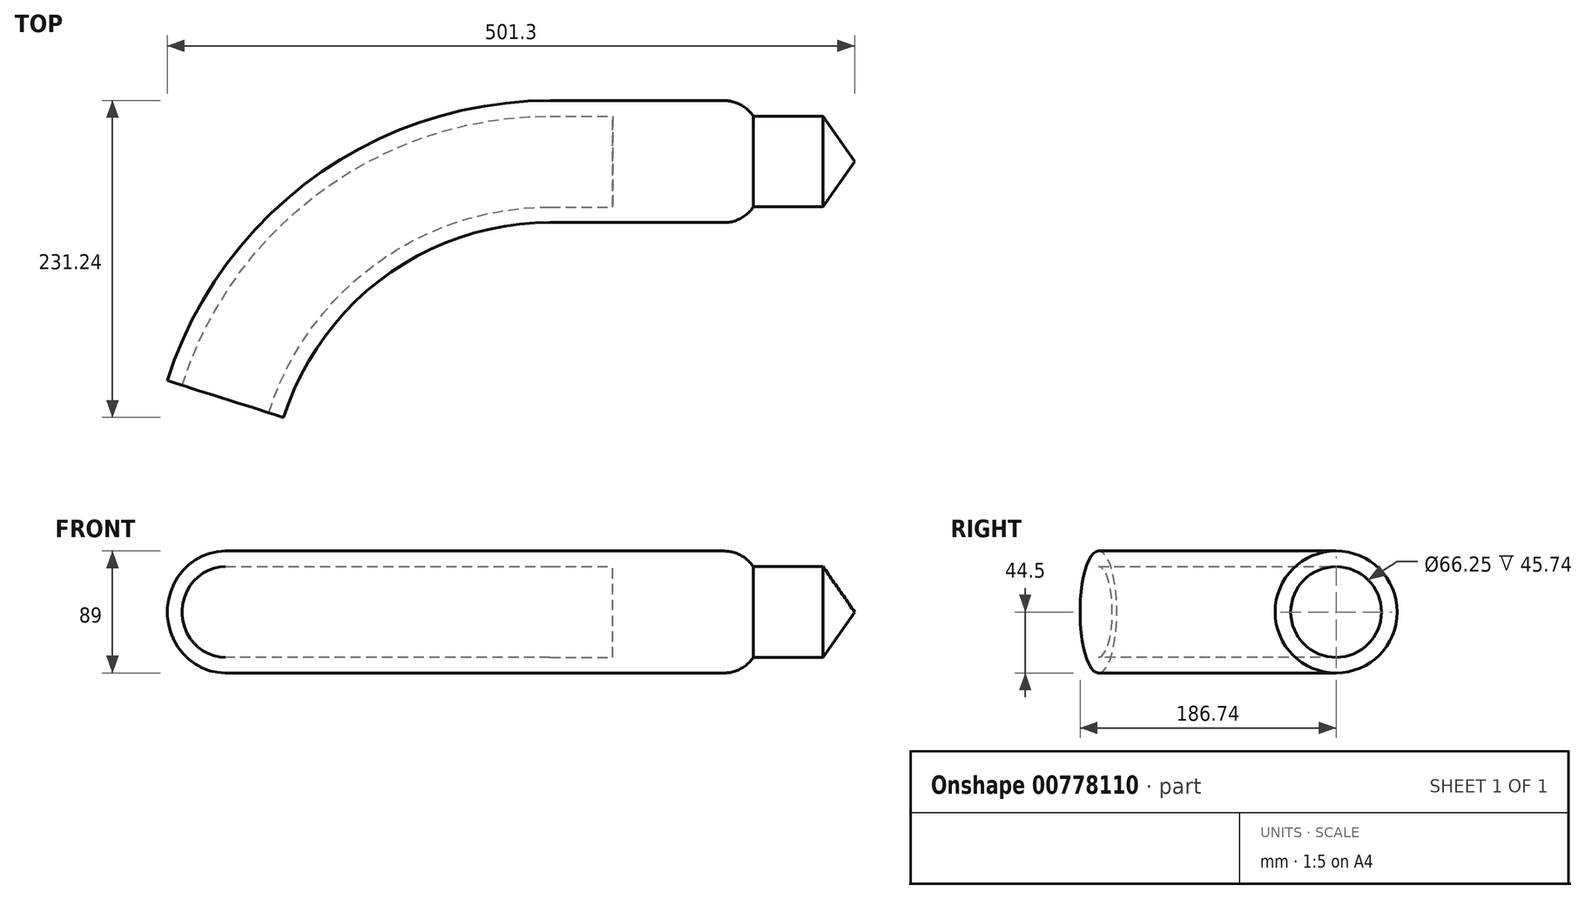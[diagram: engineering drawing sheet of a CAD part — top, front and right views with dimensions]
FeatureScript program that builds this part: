
annotation { "Feature Type Name" : "Feature", "Feature Type Description" : "" }
export const myFeature = defineFeature(function(context is Context, id is Id, definition is map)
    precondition{}
    {
        {
            var Q0;
            Q0=qCreatedBy(makeId("Front.planeOp"),FACE);
            var sketch = newSketch(context, id + "F0", { "sketchPlane" : qUnion([Q0])});
            skLineSegment(sketch, "E0", {"start": v(0, 0) * mm, "end": v(174.67, 0) * mm, "construction": true});
            skLineSegment(sketch, "E1", {"start": v(0, 33.12) * mm, "end": v(0, 44.5) * mm});
            skLineSegment(sketch, "E2", {"start": v(0, 44.5) * mm, "end": v(127.05, 44.5) * mm});
            skArc(sketch, "E3", {"start": v(127.05, 44.5) * mm, "mid": v(139.07, 41.47) * mm, "end": v(148.2, 33.1) * mm});
            skLineSegment(sketch, "E4", {"start": v(148.2, 33.1) * mm, "end": v(199.15, 33.1) * mm});
            skLineSegment(sketch, "E5", {"start": v(199.15, 33.1) * mm, "end": v(222.2, 0) * mm});
            skLineSegment(sketch, "E6", {"start": v(222.2, 0) * mm, "end": v(45.74, 0) * mm});
            skLineSegment(sketch, "E7", {"start": v(0, 33.12) * mm, "end": v(45.74, 33.12) * mm});
            skLineSegment(sketch, "E8", {"start": v(45.74, 33.12) * mm, "end": v(45.74, 0) * mm});
            skSolve(sketch);
        }
        {
            var Q0;
            Q0=makeQuery(id+"F0.imprint","IMPRINT",FACE,{"disambiguationData":[TD([[makeQuery(id+"F0.imprint","IMPRINT",EDGE,{"derivedFrom":sQuery(id+"F0.wireOp",EDGE,"E1")}),-1.0]])]});
            var Q1;
            Q1=sQuery(id+"F0.wireOp",EDGE,"E6");
            revolve(context, id + "F1", {"surfaceOperationType" : NewSurfaceOperationType.NEW, "entities" : qUnion([Q0]), "axis" : qUnion([Q1]), "revolveType" : RevolveType.FULL});
        }
        {
            var Q0;
            Q0=qCreatedBy(makeId("Top.planeOp"),FACE);
            var sketch = newSketch(context, id + "F2", { "sketchPlane" : qUnion([Q0])});
            skLineSegment(sketch, "E9", {"start": v(0, 0) * mm, "end": v(-74.8, 0) * mm, "construction": true});
            skArc(sketch, "E10", {"start": v(0, 0) * mm, "mid": v(-146.68, -47.96) * mm, "end": v(-236.69, -173.3) * mm});
            skSolve(sketch);
        }
        {
            var Q0;
            Q0=makeQuery(id+"F1.opRevolve","SWEPT_FACE",FACE,{"disambiguationData":[OSD([sQuery(id+"F0.wireOp",EDGE,"E1")])]});
            var Q1;
            Q1=sQuery(id+"F2.wireOp",EDGE,"E10");
            sweep(context, id + "F3", {"operationType" : NewBodyOperationType.ADD, "profiles" : qUnion([Q0]), "path" : qUnion([Q1])});
        }
    });
